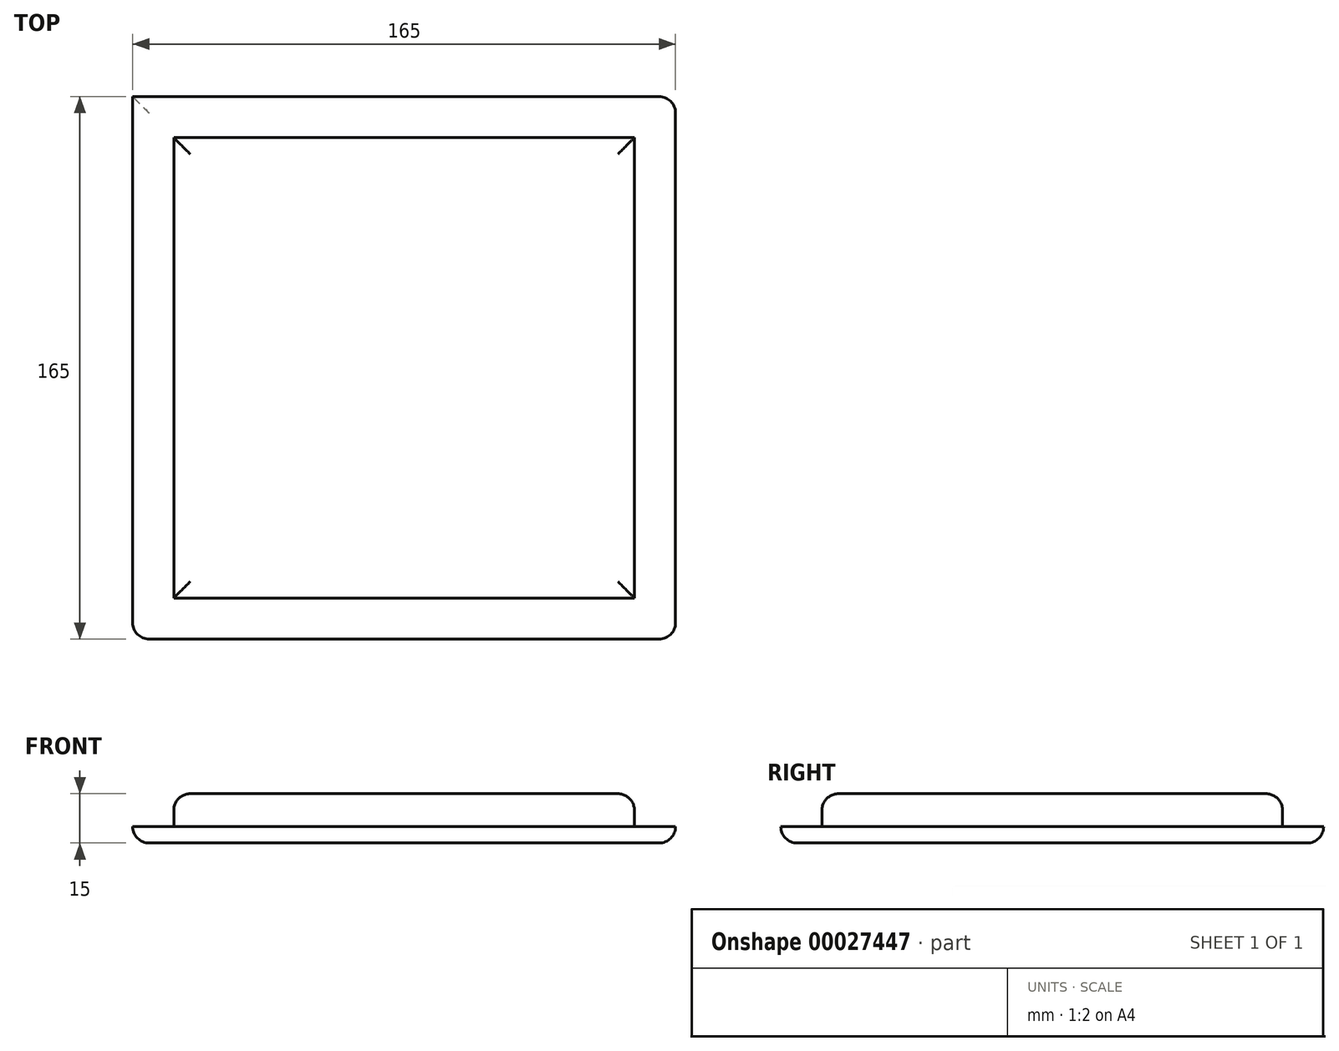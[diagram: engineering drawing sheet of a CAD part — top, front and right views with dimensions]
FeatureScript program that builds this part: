
annotation { "Feature Type Name" : "Feature", "Feature Type Description" : "" }
export const myFeature = defineFeature(function(context is Context, id is Id, definition is map)
    precondition{}
    {
        {
            var Q0;
            Q0=qCreatedBy(makeId("Top.planeOp"),FACE);
            var sketch = newSketch(context, id + "F0", { "sketchPlane" : qUnion([Q0])});
            skLineSegment(sketch, "E0.rect.bottom", {"start": v(70, 70) * mm, "end": v(-70, 70) * mm});
            skLineSegment(sketch, "E0.rect.top", {"start": v(70, -70) * mm, "end": v(-70, -70) * mm});
            skLineSegment(sketch, "E0.rect.left", {"start": v(70, 70) * mm, "end": v(70, -70) * mm});
            skLineSegment(sketch, "E0.rect.right", {"start": v(-70, 70) * mm, "end": v(-70, -70) * mm});
            skPoint(sketch, "E0.rect.middle", {"position": v(0, 0) * mm});
            skSolve(sketch);
        }
        {
            var Q0;
            Q0 = qSketchRegion(id + "F0", true);
            extrude(context, id + "F1", {"entities" : qUnion([Q0]), "oppositeDirection" : true, "depth" : 10 * mm});
        }
        {
            var Q0;
            Q0=makeQuery(id+"F1.opExtrude","CAP_FACE",FACE,{"disambiguationData":[OSD([sQuery(id+"F0.wireOp",EDGE,"E0.rect.bottom"),sQuery(id+"F0.wireOp",EDGE,"E0.rect.top"),sQuery(id+"F0.wireOp",EDGE,"E0.rect.left"),sQuery(id+"F0.wireOp",EDGE,"E0.rect.right")])],"isStart":false});
            var sketch = newSketch(context, id + "F2", { "sketchPlane" : qUnion([Q0])});
            skLineSegment(sketch, "E1.rect.bottom", {"start": v(82.5, 82.5) * mm, "end": v(-82.5, 82.5) * mm});
            skLineSegment(sketch, "E1.rect.top", {"start": v(82.5, -82.5) * mm, "end": v(-82.5, -82.5) * mm});
            skLineSegment(sketch, "E1.rect.left", {"start": v(82.5, 82.5) * mm, "end": v(82.5, -82.5) * mm});
            skLineSegment(sketch, "E1.rect.right", {"start": v(-82.5, 82.5) * mm, "end": v(-82.5, -82.5) * mm});
            skPoint(sketch, "E1.rect.middle", {"position": v(0, 0) * mm});
            skSolve(sketch);
        }
        {
            var Q0;
            Q0 = qSketchRegion(id + "F2", true);
            extrude(context, id + "F3", {"entities" : qUnion([Q0]), "operationType" : NewBodyOperationType.ADD, "depth" : 5 * mm});
        }
        {
            var Q0;
            Q0=makeQuery(id+"F3.opExtrude","SWEPT_EDGE",EDGE,{"disambiguationData":[OSD([sQuery(id+"F2.wireOp",EDGE,"E1.rect.bottom"),sQuery(id+"F2.wireOp",EDGE,"E1.rect.left")])]});
            var Q1;
            Q1=makeQuery(id+"F3.opExtrude","CAP_EDGE",EDGE,{"disambiguationData":[OSD([sQuery(id+"F2.wireOp",EDGE,"E1.rect.bottom")])],"isStart":false});
            var Q2;
            Q2=makeQuery(id+"F3.opExtrude","SWEPT_EDGE",EDGE,{"disambiguationData":[OSD([sQuery(id+"F2.wireOp",EDGE,"E1.rect.bottom"),sQuery(id+"F2.wireOp",EDGE,"E1.rect.right")])]});
            var Q3;
            Q3=makeQuery(id+"F3.opExtrude","CAP_EDGE",EDGE,{"disambiguationData":[OSD([sQuery(id+"F2.wireOp",EDGE,"E1.rect.right")])],"isStart":false});
            var Q4;
            Q4=makeQuery(id+"F3.opExtrude","CAP_EDGE",EDGE,{"disambiguationData":[OSD([sQuery(id+"F2.wireOp",EDGE,"E1.rect.top")])],"isStart":false});
            var Q5;
            Q5=makeQuery(id+"F3.opExtrude","SWEPT_EDGE",EDGE,{"disambiguationData":[OSD([sQuery(id+"F2.wireOp",EDGE,"E1.rect.top"),sQuery(id+"F2.wireOp",EDGE,"E1.rect.left")])]});
            var Q6;
            Q6=makeQuery(id+"F3.opExtrude","CAP_EDGE",EDGE,{"disambiguationData":[OSD([sQuery(id+"F2.wireOp",EDGE,"E1.rect.left")])],"isStart":false});
            fillet(context, id + "F4", {"entities" : qUnion([Q0, Q1, Q2, Q3, Q4, Q5, Q6]), "radius" : 5 * mm, "tangentPropagation" : true, "allowEdgeOverflow" : false});
        }
        {
            var Q0;
            Q0=makeQuery(id+"F1.opExtrude","CAP_EDGE",EDGE,{"disambiguationData":[OSD([sQuery(id+"F0.wireOp",EDGE,"E0.rect.top")])],"isStart":true});
            var Q1;
            Q1=makeQuery(id+"F1.opExtrude","CAP_EDGE",EDGE,{"disambiguationData":[OSD([sQuery(id+"F0.wireOp",EDGE,"E0.rect.left")])],"isStart":true});
            var Q2;
            Q2=makeQuery(id+"F1.opExtrude","CAP_EDGE",EDGE,{"disambiguationData":[OSD([sQuery(id+"F0.wireOp",EDGE,"E0.rect.right")])],"isStart":true});
            var Q3;
            Q3=makeQuery(id+"F1.opExtrude","CAP_EDGE",EDGE,{"disambiguationData":[OSD([sQuery(id+"F0.wireOp",EDGE,"E0.rect.bottom")])],"isStart":true});
            fillet(context, id + "F5", {"entities" : qUnion([Q0, Q1, Q2, Q3]), "radius" : 5 * mm, "tangentPropagation" : true, "allowEdgeOverflow" : false});
        }
    });
